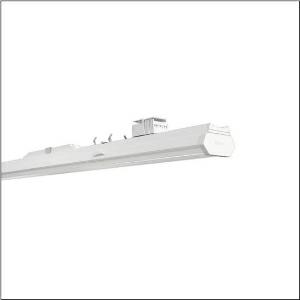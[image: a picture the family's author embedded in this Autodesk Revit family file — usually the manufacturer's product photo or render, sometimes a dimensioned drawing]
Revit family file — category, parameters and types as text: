
# Revit family: licross_r__11_protected_extreme_ho_51tp11dn4exre_51ee
name_source: partatom
category: Lighting Fixtures
units: mm (PartAtom-declared; Revit-internal decimal feet)

## family parameters
Cut with Voids When Loaded = No
Host = Face
Light Source = No
Part Type = Normal
Room Calculation Point = No
Round Connector Dimension = Use Diameter
Shared = No

## types (1)
- --- (1 x LED, 14140 lm, 84.2 W, 4000K)
    Apparent Load = 84 VA
    CIE Flux Codes = 84 94 98 99 100
    Color Rendering = 80
    Color Temperature = 4000K
    Default Elevation = 1800 mm
    Description = Licross® 11 Protected extreme HOluminaire insert, length: 1.500mm, width: 90mm, height: 101mm, LED rated luminous flux: 14.140lm, light colour: 840, control gear: DALI 2, control gear: ECG DALI, with plug, 5-pole, with phase selection, mains connection: 220..240V, AC, 50/60Hz, halogen-free wiring, primary optical cover: cover, of PMMA, light emission: direct with ceiling illumination distribution, protection rating (complete): IP64, insulation class (complete): insulation class I (protective earthing), certification: CE, ENEC, VDE, protection symbol: D if used in an environment with conductive dust loads with corresponding accessories, permissible ambient temperature for indoor applications: -25..+45°C, reducing of maximum allowable ambient temperature of 5°C with ceiling mounting, corresponds to IFS (International Featured Standards) requirements for safety and quality in the food industry, packaging unit: 1 piece
    Height = 92 mm
    Lamp = 1 x LED
    Lamp Light Flux = 14140 lm
    Lamp Power = 84.2 W
    Lamp count = 1
    Length = 1500 mm
    Luminous efficacy = 168 lm/W
    Manufacturer = Siteco
    ModVariant = No
    Model = 51TP11DN4EXRE
    Mounting Place = Ceiling
    Mounting Type = Pendant
    Number of Poles = 1
    OnlyDefault = Yes
    Power Factor = 1
    Product Name = Licross® 11 Protected extreme HO
    Product group = luminaire insert
    ProductGroupID = 902
    Protection Class = Protection class I
    Protection Degree = IP 64
    RLX_Detail_Level = 1
    RlxData = <blob elided: 23869 chars, md5=b568cd19>
    Socket = socket
    Standby Power = 0 W
    System Light Flux = 14140 lm
    System Power = 84 W
    Type Comments = factory setting: luminous flux: 100 % | dim-lin: 254 | 475 mA
    Type Image = l_1256148.jpg
    URL = http://relux.com
    VarID = @adj_132714
    Voltage = 0 V
    Weight = 0.00 kg
    Width = 88 mm

## geometry (parser evidence)
native form markers: Blend x4, Sweep x12
no freeform markers — native parametric forms only
